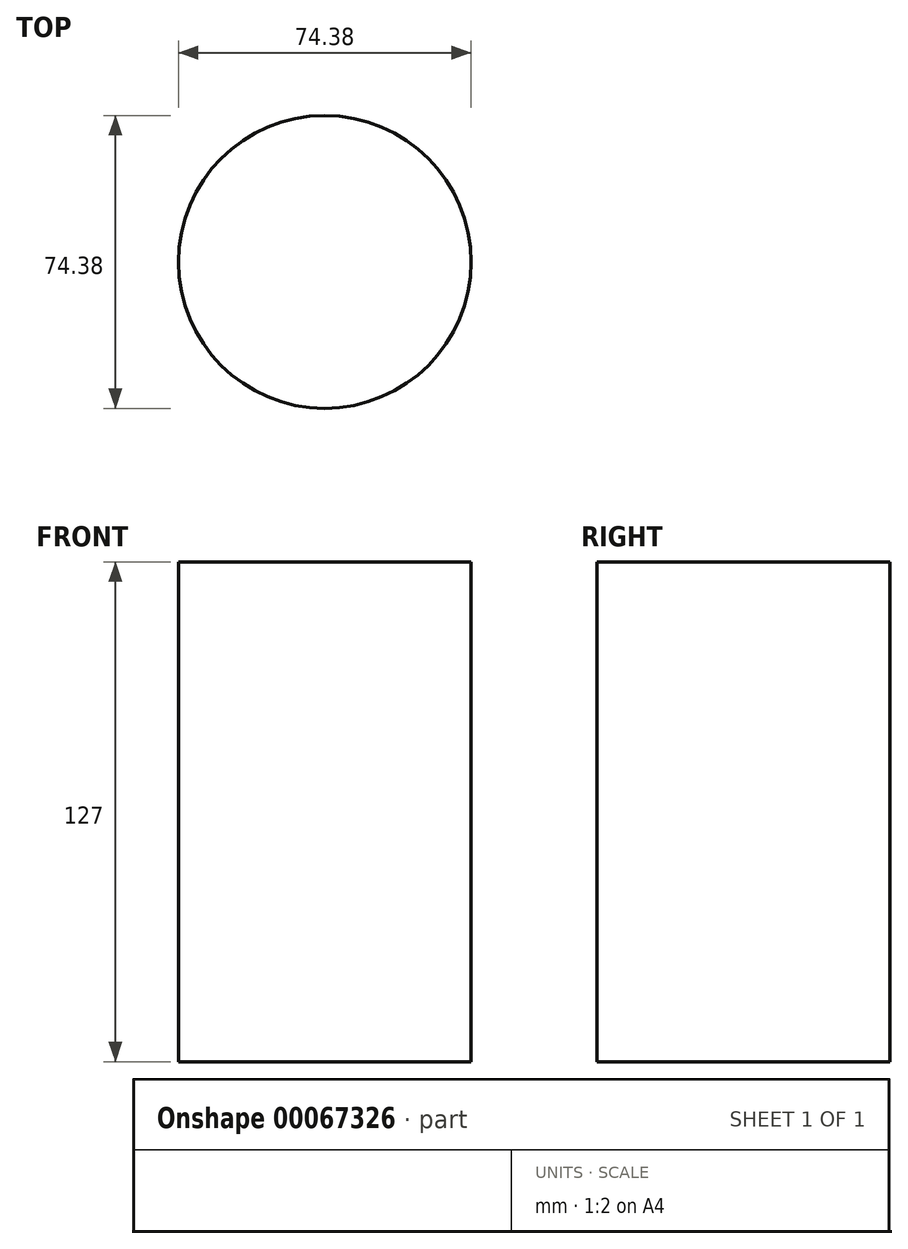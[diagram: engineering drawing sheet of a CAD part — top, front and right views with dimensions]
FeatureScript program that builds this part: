
annotation { "Feature Type Name" : "Feature", "Feature Type Description" : "" }
export const myFeature = defineFeature(function(context is Context, id is Id, definition is map)
    precondition{}
    {
        {
            var Q0;
            Q0=qCreatedBy(makeId("Top.planeOp"),FACE);
            var sketch = newSketch(context, id + "F0", { "sketchPlane" : qUnion([Q0])});
            skLineSegment(sketch, "E0.rect.bottom", {"start": v(-53.91, -37.2) * mm, "end": v(53.91, -37.2) * mm});
            skLineSegment(sketch, "E0.rect.top", {"start": v(-53.91, 37.2) * mm, "end": v(53.91, 37.2) * mm});
            skLineSegment(sketch, "E0.rect.left", {"start": v(-53.91, -37.2) * mm, "end": v(-53.91, 37.2) * mm});
            skLineSegment(sketch, "E0.rect.right", {"start": v(53.91, -37.2) * mm, "end": v(53.91, 37.2) * mm});
            skPoint(sketch, "E0.rect.middle", {"position": v(0, 0) * mm});
            skSolve(sketch);
        }
        {
            var Q0;
            Q0=makeQuery(id+"F0.imprint","IMPRINT",FACE,{"disambiguationData":[TD([[makeQuery(id+"F0.imprint","IMPRINT",EDGE,{"derivedFrom":sQuery(id+"F0.wireOp",EDGE,"E0.rect.bottom")}),1.0]])]});
            extrude(context, id + "F1", {"entities" : qUnion([Q0]), "endBound" : BoundingType.SYMMETRIC, "depth" : 127 * mm});
        }
        {
            var Q0;
            Q0=makeQuery(id+"F1.opExtrude","CAP_FACE",FACE,{"disambiguationData":[OSD([sQuery(id+"F0.wireOp",EDGE,"E0.rect.bottom"),sQuery(id+"F0.wireOp",EDGE,"E0.rect.top"),sQuery(id+"F0.wireOp",EDGE,"E0.rect.left"),sQuery(id+"F0.wireOp",EDGE,"E0.rect.right")])],"isStart":false});
            var sketch = newSketch(context, id + "F2", { "sketchPlane" : qUnion([Q0])});
            skCircle(sketch, "E1", {"center": v(0, 0) * mm, "radius": 37.2 * mm});
            skSolve(sketch);
        }
        {
            var Q0;
            {var subQ5=makeQuery(id+"F1.opExtrude","CAP_EDGE",EDGE,{"disambiguationData":[OSD([sQuery(id+"F0.wireOp",EDGE,"E0.rect.left")])],"isStart":false});Q0=makeQuery(id+"F2.imprint","IMPRINT",FACE,{"disambiguationData":[TD([[makeQuery(id+"F2.imprint","IMPRINT",EDGE,{"derivedFrom":subQ5}),-1.0]])]});}
            var Q1;
            {var subQ5=makeQuery(id+"F1.opExtrude","CAP_EDGE",EDGE,{"disambiguationData":[OSD([sQuery(id+"F0.wireOp",EDGE,"E0.rect.right")])],"isStart":false});Q1=makeQuery(id+"F2.imprint","IMPRINT",FACE,{"disambiguationData":[TD([[makeQuery(id+"F2.imprint","IMPRINT",EDGE,{"derivedFrom":subQ5}),1.0]])]});}
            extrude(context, id + "F3", {"entities" : qUnion([Q0, Q1]), "operationType" : NewBodyOperationType.REMOVE, "endBound" : BoundingType.THROUGH_ALL, "oppositeDirection" : true, "depth" : 25.4 * mm});
        }
    });
